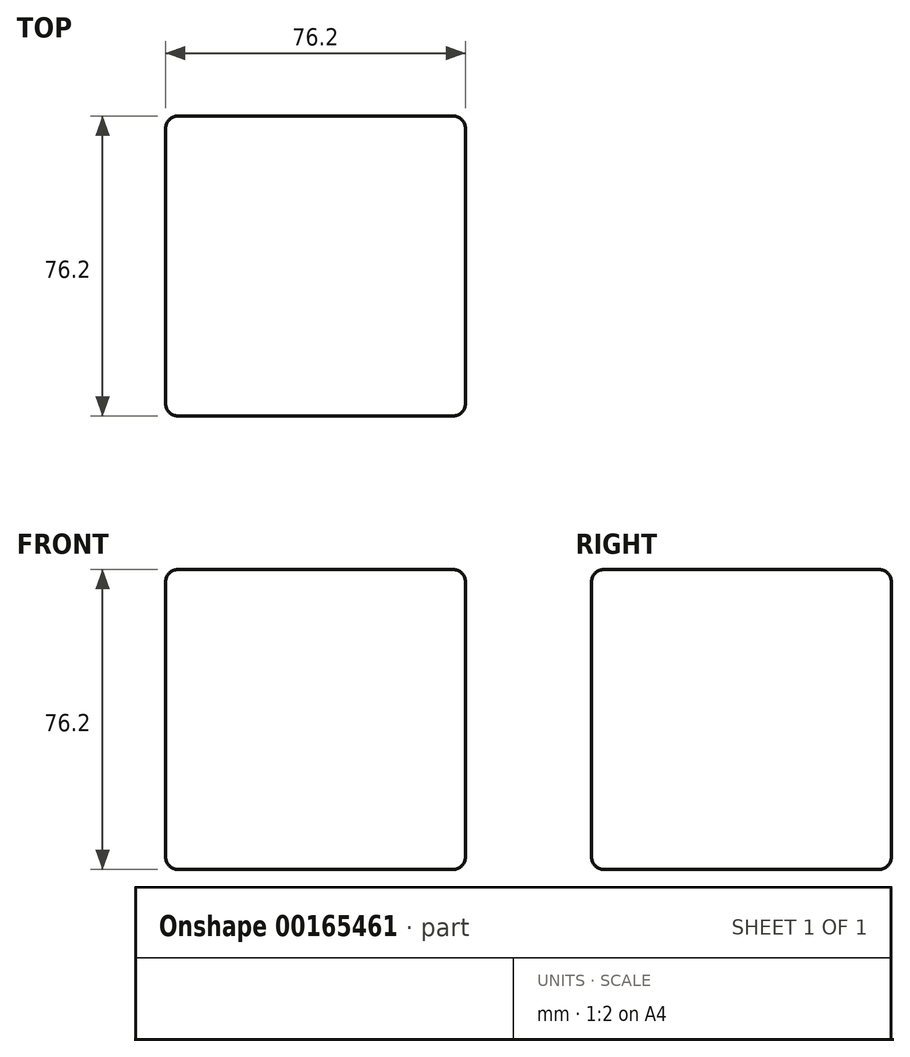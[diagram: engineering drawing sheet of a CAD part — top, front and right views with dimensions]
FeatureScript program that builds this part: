
annotation { "Feature Type Name" : "Feature", "Feature Type Description" : "" }
export const myFeature = defineFeature(function(context is Context, id is Id, definition is map)
    precondition{}
    {
        {
            var Q0;
            Q0=qCreatedBy(makeId("Front.planeOp"),FACE);
            var sketch = newSketch(context, id + "F0", { "sketchPlane" : qUnion([Q0])});
            skLineSegment(sketch, "E0.bottom", {"start": v(-34.93, 38.1) * mm, "end": v(34.93, 38.1) * mm});
            skLineSegment(sketch, "E0.top", {"start": v(-34.92, -38.1) * mm, "end": v(34.92, -38.1) * mm});
            skLineSegment(sketch, "E0.left", {"start": v(-38.1, 34.93) * mm, "end": v(-38.1, -34.93) * mm});
            skLineSegment(sketch, "E0.right", {"start": v(38.1, 34.93) * mm, "end": v(38.1, -34.93) * mm});
            skPoint(sketch, "E0.middle", {"position": v(0, 0) * mm});
            skPoint(sketch, "E1.visualSharp", {"position": v(38.1, 38.1) * mm});
            skArc(sketch, "E1.filletArc", {"start": v(38.1, 34.93) * mm, "mid": v(37.17, 37.17) * mm, "end": v(34.93, 38.1) * mm});
            skPoint(sketch, "E2.visualSharp", {"position": v(38.1, -38.1) * mm});
            skArc(sketch, "E2.filletArc", {"start": v(34.92, -38.1) * mm, "mid": v(37.17, -37.17) * mm, "end": v(38.1, -34.93) * mm});
            skPoint(sketch, "E3.visualSharp", {"position": v(-38.1, 38.1) * mm});
            skArc(sketch, "E3.filletArc", {"start": v(-34.93, 38.1) * mm, "mid": v(-37.17, 37.17) * mm, "end": v(-38.1, 34.93) * mm});
            skPoint(sketch, "E4.visualSharp", {"position": v(-38.1, -38.1) * mm});
            skArc(sketch, "E4.filletArc", {"start": v(-38.1, -34.93) * mm, "mid": v(-37.17, -37.17) * mm, "end": v(-34.93, -38.1) * mm});
            skSolve(sketch);
        }
        {
            var Q0;
            Q0 = qSketchRegion(id + "F0", true);
            extrude(context, id + "F1", {"entities" : qUnion([Q0]), "depth" : 76.2 * mm});
        }
        {
            var Q0;
            Q0=makeQuery(id+"F1.opExtrude","CAP_EDGE",EDGE,{"disambiguationData":[OSD([sQuery(id+"F0.wireOp",EDGE,"E0.bottom")])],"isStart":false});
            var Q1;
            Q1=makeQuery(id+"F1.opExtrude","CAP_EDGE",EDGE,{"disambiguationData":[OSD([sQuery(id+"F0.wireOp",EDGE,"E0.left")])],"isStart":false});
            var Q2;
            Q2=makeQuery(id+"F1.opExtrude","CAP_EDGE",EDGE,{"disambiguationData":[OSD([sQuery(id+"F0.wireOp",EDGE,"E0.top")])],"isStart":false});
            var Q3;
            Q3=makeQuery(id+"F1.opExtrude","CAP_EDGE",EDGE,{"disambiguationData":[OSD([sQuery(id+"F0.wireOp",EDGE,"E0.right")])],"isStart":false});
            var Q4;
            Q4=makeQuery(id+"F1.opExtrude","CAP_EDGE",EDGE,{"disambiguationData":[OSD([sQuery(id+"F0.wireOp",EDGE,"E0.left")])],"isStart":true});
            fillet(context, id + "F2", {"entities" : qUnion([Q0, Q1, Q2, Q3, Q4]), "radius" : 3.17 * mm, "tangentPropagation" : true, "allowEdgeOverflow" : false});
        }
    });
